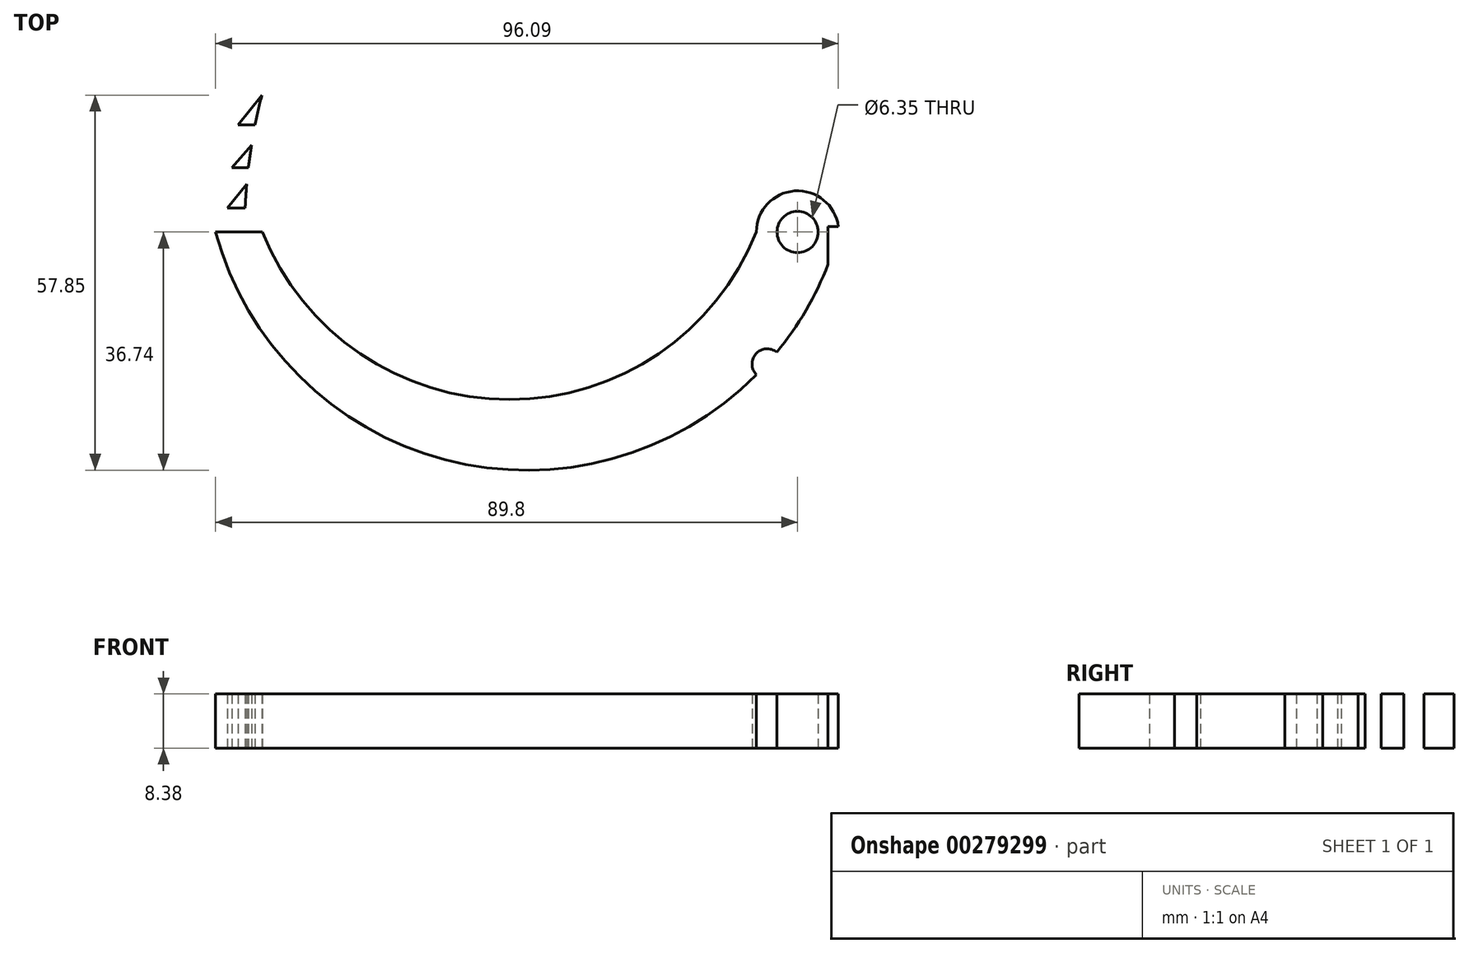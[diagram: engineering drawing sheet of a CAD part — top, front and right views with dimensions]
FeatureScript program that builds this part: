
annotation { "Feature Type Name" : "Feature", "Feature Type Description" : "" }
export const myFeature = defineFeature(function(context is Context, id is Id, definition is map)
    precondition{}
    {
        {
            var Q0;
            Q0=qCreatedBy(makeId("Top.planeOp"),FACE);
            var sketch = newSketch(context, id + "F0", { "sketchPlane" : qUnion([Q0])});
            skArc(sketch, "E0", {"start": v(-76.2, 0) * mm, "mid": v(-38.1, -25.85) * mm, "end": v(0, 0) * mm});
            skCircle(sketch, "E1", {"center": v(6.35, 0) * mm, "radius": 6.35 * mm});
            skArc(sketch, "E2", {"start": v(-83.45, 0) * mm, "mid": v(-35.38, -36.74) * mm, "end": v(12.7, 0) * mm});
            skLineSegment(sketch, "E3", {"start": v(-83.45, 0) * mm, "end": v(-74.45, 0) * mm});
            skArc(sketch, "E4", {"start": v(-76.2, 0) * mm, "mid": v(-75.51, 10.64) * mm, "end": v(-73.46, 21.1) * mm});
            skArc(sketch, "E5", {"start": v(-78.95, 0) * mm, "mid": v(-78.28, 10.64) * mm, "end": v(-76.3, 21.1) * mm});
            skLineSegment(sketch, "E6", {"start": v(-76.3, 21.1) * mm, "end": v(-73.46, 21.1) * mm});
            skLineSegment(sketch, "E7", {"start": v(-76.3, 21.1) * mm, "end": v(-79.97, 16.51) * mm});
            skLineSegment(sketch, "E8", {"start": v(-79.97, 16.51) * mm, "end": v(-77.34, 16.51) * mm});
            skLineSegment(sketch, "E9", {"start": v(-77.9, 13.38) * mm, "end": v(-80.9, 9.9) * mm});
            skLineSegment(sketch, "E10", {"start": v(-80.9, 9.9) * mm, "end": v(-78.37, 9.9) * mm});
            skLineSegment(sketch, "E11", {"start": v(-78.63, 7.4) * mm, "end": v(-81.6, 3.73) * mm});
            skLineSegment(sketch, "E12", {"start": v(-81.6, 3.73) * mm, "end": v(-78.87, 3.73) * mm});
            skCircle(sketch, "E13", {"center": v(6.35, 0) * mm, "radius": 3.18 * mm});
            skArc(sketch, "E14", {"start": v(3.13, -18.54) * mm, "mid": v(-0.08, -18.79) * mm, "end": v(0, -22) * mm});
            skSolve(sketch);
        }
        {
            var Q0;
            {var subQ0=sQuery(id+"F0.wireOp",EDGE,"E2");var subQ1=sQuery(id+"F0.wireOp",EDGE,"E1");var subQ2=makeQuery(id+"F0.imprint","INTERSECT",VERTEX,{"disambiguationData":[OD(0.0)],"derivedFrom":[subQ1,subQ0]});Q0=makeQuery(id+"F0.imprint","IMPRINT",FACE,{"disambiguationData":[TD([[makeQuery(id+"F0.imprint","IMPRINT",EDGE,{"disambiguationData":[TD([[subQ2,1.0]])],"derivedFrom":subQ1}),1.0]])]});}
            var Q1;
            {var subQ0=sQuery(id+"F0.wireOp",EDGE,"E11");Q1=makeQuery(id+"F0.imprint","IMPRINT",FACE,{"disambiguationData":[TD([[makeQuery(id+"F0.imprint","IMPRINT",EDGE,{"derivedFrom":subQ0}),1.0]])]});}
            var Q2;
            {var subQ0=sQuery(id+"F0.wireOp",EDGE,"E9");Q2=makeQuery(id+"F0.imprint","IMPRINT",FACE,{"disambiguationData":[TD([[makeQuery(id+"F0.imprint","IMPRINT",EDGE,{"derivedFrom":subQ0}),1.0]])]});}
            var Q3;
            {var subQ0=sQuery(id+"F0.wireOp",EDGE,"E7");Q3=makeQuery(id+"F0.imprint","IMPRINT",FACE,{"disambiguationData":[TD([[makeQuery(id+"F0.imprint","IMPRINT",EDGE,{"derivedFrom":subQ0}),1.0]])]});}
            var Q4;
            Q4=makeQuery(id+"F0.imprint","IMPRINT",FACE,{"disambiguationData":[TD([[makeQuery(id+"F0.imprint","IMPRINT",EDGE,{"derivedFrom":sQuery(id+"F0.wireOp",EDGE,"E13")}),-1.0]])]});
            var Q5;
            {var subQ5=sQuery(id+"F0.wireOp",EDGE,"E4");Q5=makeQuery(id+"F0.imprint","IMPRINT",FACE,{"disambiguationData":[TD([[makeQuery(id+"F0.imprint","IMPRINT",EDGE,{"derivedFrom":subQ5}),1.0]])]});}
            var Q6;
            {var subQ6=sQuery(id+"F0.wireOp",EDGE,"E0");Q6=makeQuery(id+"F0.imprint","IMPRINT",FACE,{"disambiguationData":[TD([[makeQuery(id+"F0.imprint","IMPRINT",EDGE,{"derivedFrom":subQ6}),-1.0]])]});}
            extrude(context, id + "F1", {"entities" : qUnion([Q0, Q1, Q2, Q3, Q4, Q5, Q6]), "depth" : 8.38 * mm});
        }
        {
            var Q0;
            Q0=makeQuery(id+"F1.opExtrude","CAP_FACE",FACE,{"disambiguationData":[OSD([sQuery(id+"F0.wireOp",EDGE,"E0"),sQuery(id+"F0.wireOp",EDGE,"E1"),sQuery(id+"F0.wireOp",EDGE,"E2"),sQuery(id+"F0.wireOp",EDGE,"E3"),sQuery(id+"F0.wireOp",EDGE,"E4"),sQuery(id+"F0.wireOp",EDGE,"E5"),sQuery(id+"F0.wireOp",EDGE,"E6"),sQuery(id+"F0.wireOp",EDGE,"E7"),sQuery(id+"F0.wireOp",EDGE,"E8"),sQuery(id+"F0.wireOp",EDGE,"E9"),sQuery(id+"F0.wireOp",EDGE,"E10"),sQuery(id+"F0.wireOp",EDGE,"E11"),sQuery(id+"F0.wireOp",EDGE,"E12"),sQuery(id+"F0.wireOp",EDGE,"E13")])],"isStart":false});
            var sketch = newSketch(context, id + "F2", { "sketchPlane" : qUnion([Q0])});
            skLineSegment(sketch, "E15.bottom", {"start": v(11.56, 0.87) * mm, "end": v(17.58, 0.87) * mm});
            skLineSegment(sketch, "E15.top", {"start": v(11.56, -10.2) * mm, "end": v(17.58, -10.2) * mm});
            skLineSegment(sketch, "E15.left", {"start": v(11.56, 0.87) * mm, "end": v(11.56, -10.2) * mm});
            skLineSegment(sketch, "E15.right", {"start": v(17.58, 0.87) * mm, "end": v(17.58, -10.2) * mm});
            skLineSegment(sketch, "E16", {"start": v(11.56, 0.87) * mm, "end": v(11.06, 0.87) * mm});
            skLineSegment(sketch, "E17", {"start": v(11.06, 0.87) * mm, "end": v(11.06, -10.24) * mm});
            skLineSegment(sketch, "E18", {"start": v(11.06, -10.24) * mm, "end": v(11.56, -10.2) * mm});
            skSolve(sketch);
        }
        {
            var Q0;
            Q0 = qSketchRegion(id + "F2", true);
            extrude(context, id + "F3", {"entities" : qUnion([Q0]), "operationType" : NewBodyOperationType.REMOVE, "oppositeDirection" : true, "depth" : 25.4 * mm});
        }
    });
